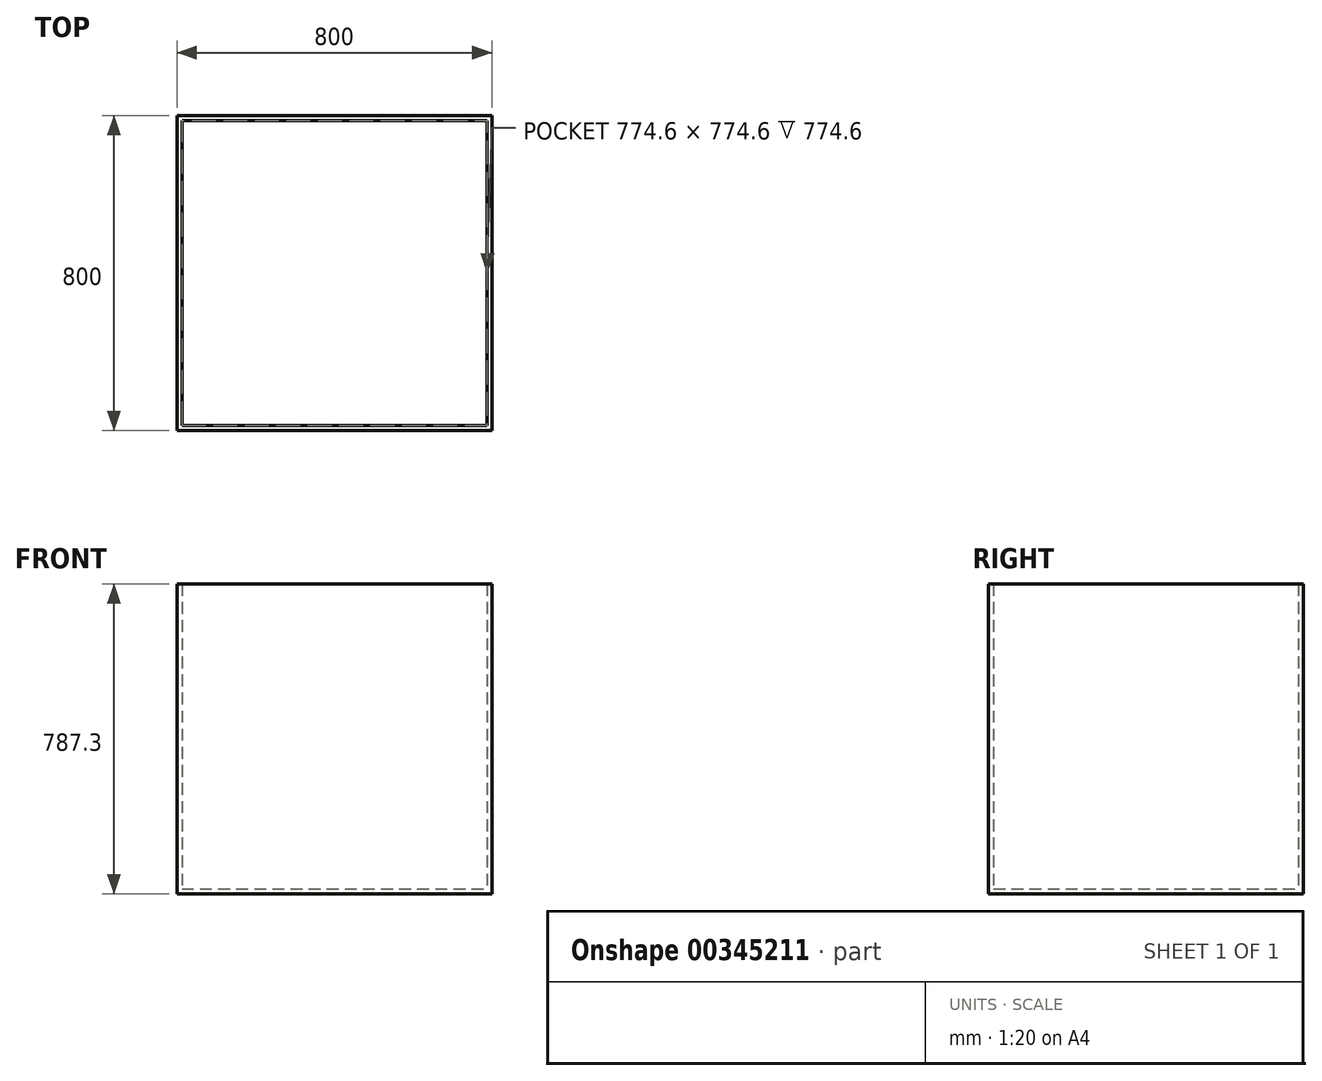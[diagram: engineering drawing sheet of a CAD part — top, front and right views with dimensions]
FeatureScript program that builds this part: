
annotation { "Feature Type Name" : "Feature", "Feature Type Description" : "" }
export const myFeature = defineFeature(function(context is Context, id is Id, definition is map)
    precondition{}
    {
        {
            var Q0;
            Q0=qCreatedBy(makeId("Front.planeOp"),FACE);
            var sketch = newSketch(context, id + "F0", { "sketchPlane" : qUnion([Q0])});
            skLineSegment(sketch, "E0.bottom", {"start": v(-332.68, 484.02) * mm, "end": v(467.32, 484.02) * mm});
            skLineSegment(sketch, "E0.top", {"start": v(-332.68, -315.98) * mm, "end": v(467.32, -315.98) * mm});
            skLineSegment(sketch, "E0.left", {"start": v(-332.68, 484.02) * mm, "end": v(-332.68, -315.98) * mm});
            skLineSegment(sketch, "E0.right", {"start": v(467.32, 484.02) * mm, "end": v(467.32, -315.98) * mm});
            skSolve(sketch);
        }
        {
            var Q0;
            Q0=makeQuery(id+"F0.imprint","IMPRINT",FACE,{"disambiguationData":[TD([[makeQuery(id+"F0.imprint","IMPRINT",EDGE,{"derivedFrom":sQuery(id+"F0.wireOp",EDGE,"E0.bottom")}),-1.0]])]});
            extrude(context, id + "F1", {"entities" : qUnion([Q0]), "endBound" : BoundingType.SYMMETRIC, "depth" : 800 * mm, "offsetDistance" : 25.4 * mm});
        }
        {
            var Q0;
            Q0=makeQuery(id+"F1.opExtrude","SWEPT_FACE",FACE,{"disambiguationData":[OSD([sQuery(id+"F0.wireOp",EDGE,"E0.bottom")])]});
            var Q1;
            Q1=makeQuery(id+"F1.opExtrude","SWEPT_BODY",BODY,{"disambiguationData":[OSD([sQuery(id+"F0.wireOp",EDGE,"E0.bottom"),sQuery(id+"F0.wireOp",EDGE,"E0.top"),sQuery(id+"F0.wireOp",EDGE,"E0.left"),sQuery(id+"F0.wireOp",EDGE,"E0.right")])]});
            shell(context, id + "F2", {"isHollow" : true, "entities" : qUnion([Q0]), "parts" : qUnion([Q1]), "thickness" : 12.7 * mm});
        }
        {
            var Q0;
            Q0=makeQuery(id+"F1.opExtrude","SWEPT_FACE",FACE,{"disambiguationData":[OSD([sQuery(id+"F0.wireOp",EDGE,"E0.bottom")])]});
            var sketch = newSketch(context, id + "F3", { "sketchPlane" : qUnion([Q0])});
            skLineSegment(sketch, "E1.bottom", {"start": v(-331.57, -400) * mm, "end": v(468.43, -400) * mm});
            skLineSegment(sketch, "E1.top", {"start": v(-331.57, 400) * mm, "end": v(468.43, 400) * mm});
            skLineSegment(sketch, "E1.left", {"start": v(-331.57, -400) * mm, "end": v(-331.57, 400) * mm});
            skLineSegment(sketch, "E1.right", {"start": v(468.43, -400) * mm, "end": v(468.43, 400) * mm});
            skPoint(sketch, "E1.middle", {"position": v(68.43, 0) * mm});
            skSolve(sketch);
        }
        {
            var Q0;
            {var subQ0=sQuery(id+"F0.wireOp",EDGE,"E0.bottom");Q0=makeQuery(id+"F3.imprint","IMPRINT",FACE,{"disambiguationData":[TD([[makeQuery(id+"F3.imprint","IMPRINT",EDGE,{"derivedFrom":makeQuery(id+"F1.opExtrude","CAP_EDGE",EDGE,{"disambiguationData":[OSD([subQ0])],"isStart":true})}),-1.0]])]});}
            var Q1;
            {var subQ3=sQuery(id+"F3.wireOp",EDGE,"E1.left");Q1=makeQuery(id+"F3.imprint","IMPRINT",FACE,{"disambiguationData":[TD([[makeQuery(id+"F3.imprint","IMPRINT",EDGE,{"derivedFrom":subQ3}),-1.0]])]});}
            extrude(context, id + "F4", {"entities" : qUnion([Q0, Q1]), "operationType" : NewBodyOperationType.REMOVE, "oppositeDirection" : true, "depth" : 12.7 * mm, "offsetDistance" : 25.4 * mm});
        }
    });
